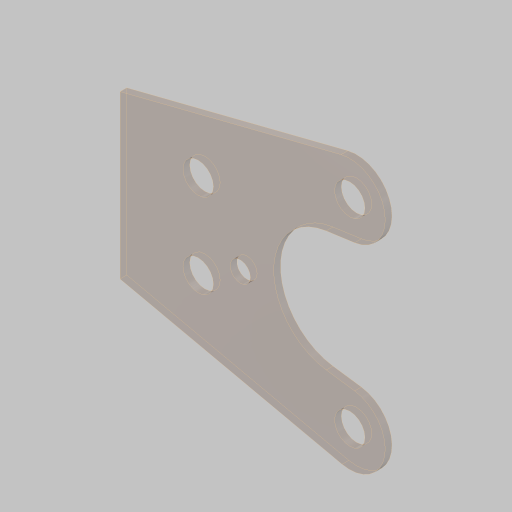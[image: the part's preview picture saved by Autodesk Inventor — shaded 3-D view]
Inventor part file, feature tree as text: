
AUTODESK INVENTOR PART (.ipt)
format: ipt  version: 2023.5 (Build 275446000, 446)  size: 150,016 bytes
history: native  units: in
note: dims shown in document units (in); Inventor stores cm internally (conversion verified against a paired STEP export)
features: extrude x1, sketch x1
ambient origin geometry x8: Origin, YZ Plane, XZ Plane, XY Plane, X Axis, Y Axis, Z Axis, Center Point
bodies: Solid1 (feature_tree)
feature tree (2):
  extrude  "Extrusion1"  Depth=0.25in
  sketch  "Sketch1"  dims[d0=3.0in d1=3.0in d2=4.5in d3=0.75in d4=7.3485in d5=1.125in d6=0.75in d7=1.128in d8=1.88in d9=3.125in d10=5.6076in d11=5.992in d12=1.125in d13=0.4688in d14=0.75in d15=1.0in d16=1.9685in d18=360.0deg d20=0.1875in d21=1.5in d22=1.0in d23=6.0in d24=8.5in d25=60.0deg d26=5.0in d27=0.25in d28=0.0in]
